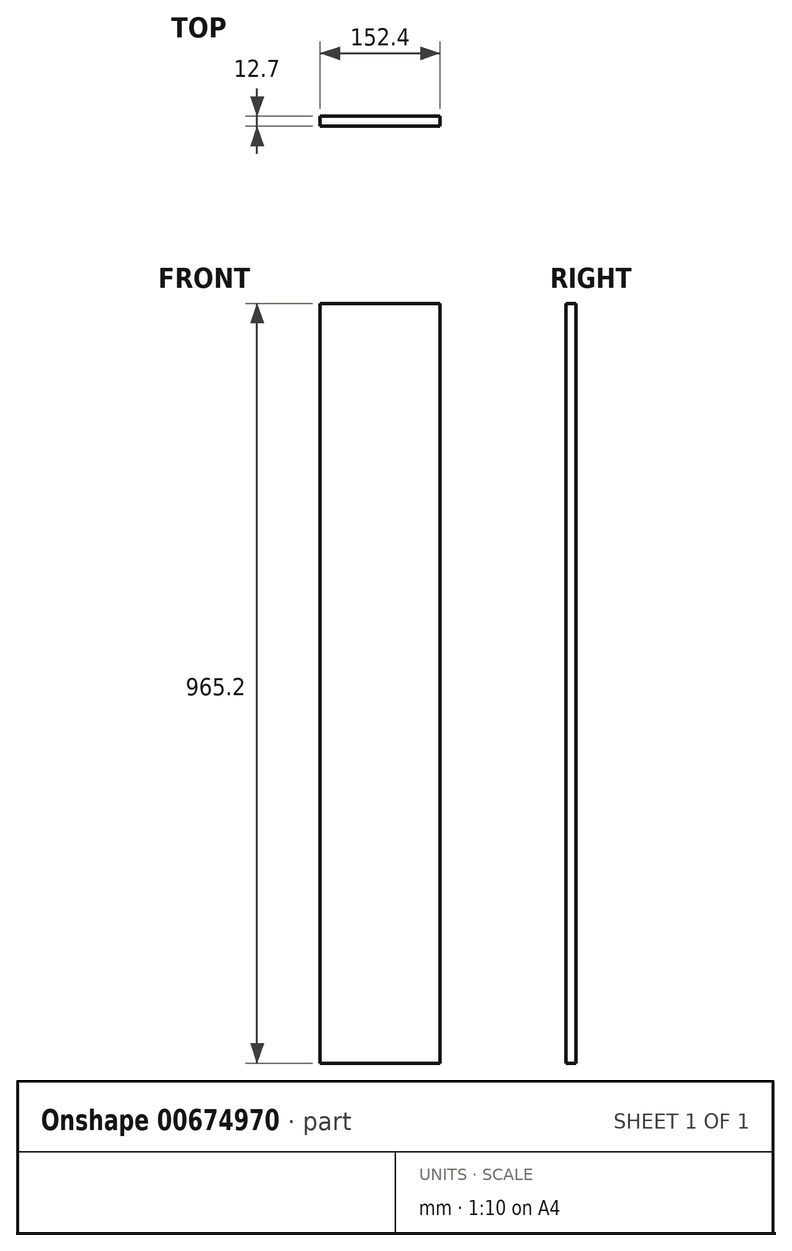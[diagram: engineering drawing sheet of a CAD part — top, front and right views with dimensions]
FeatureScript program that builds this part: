
annotation { "Feature Type Name" : "Feature", "Feature Type Description" : "" }
export const myFeature = defineFeature(function(context is Context, id is Id, definition is map)
    precondition{}
    {
        {
            var Q0;
            Q0=qCreatedBy(makeId("Front.planeOp"),FACE);
            var sketch = newSketch(context, id + "F0", { "sketchPlane" : qUnion([Q0])});
            skLineSegment(sketch, "E0.bottom", {"start": v(0, 0) * mm, "end": v(152.4, 0) * mm});
            skLineSegment(sketch, "E0.top", {"start": v(0, 965.2) * mm, "end": v(152.4, 965.2) * mm});
            skLineSegment(sketch, "E0.left", {"start": v(0, 0) * mm, "end": v(0, 965.2) * mm});
            skLineSegment(sketch, "E0.right", {"start": v(152.4, 0) * mm, "end": v(152.4, 965.2) * mm});
            skSolve(sketch);
        }
        {
            var Q0;
            Q0 = qSketchRegion(id + "F0", true);
            extrude(context, id + "F1", {"entities" : qUnion([Q0]), "depth" : 12.7 * mm, "offsetDistance" : 25.4 * mm});
        }
    });
